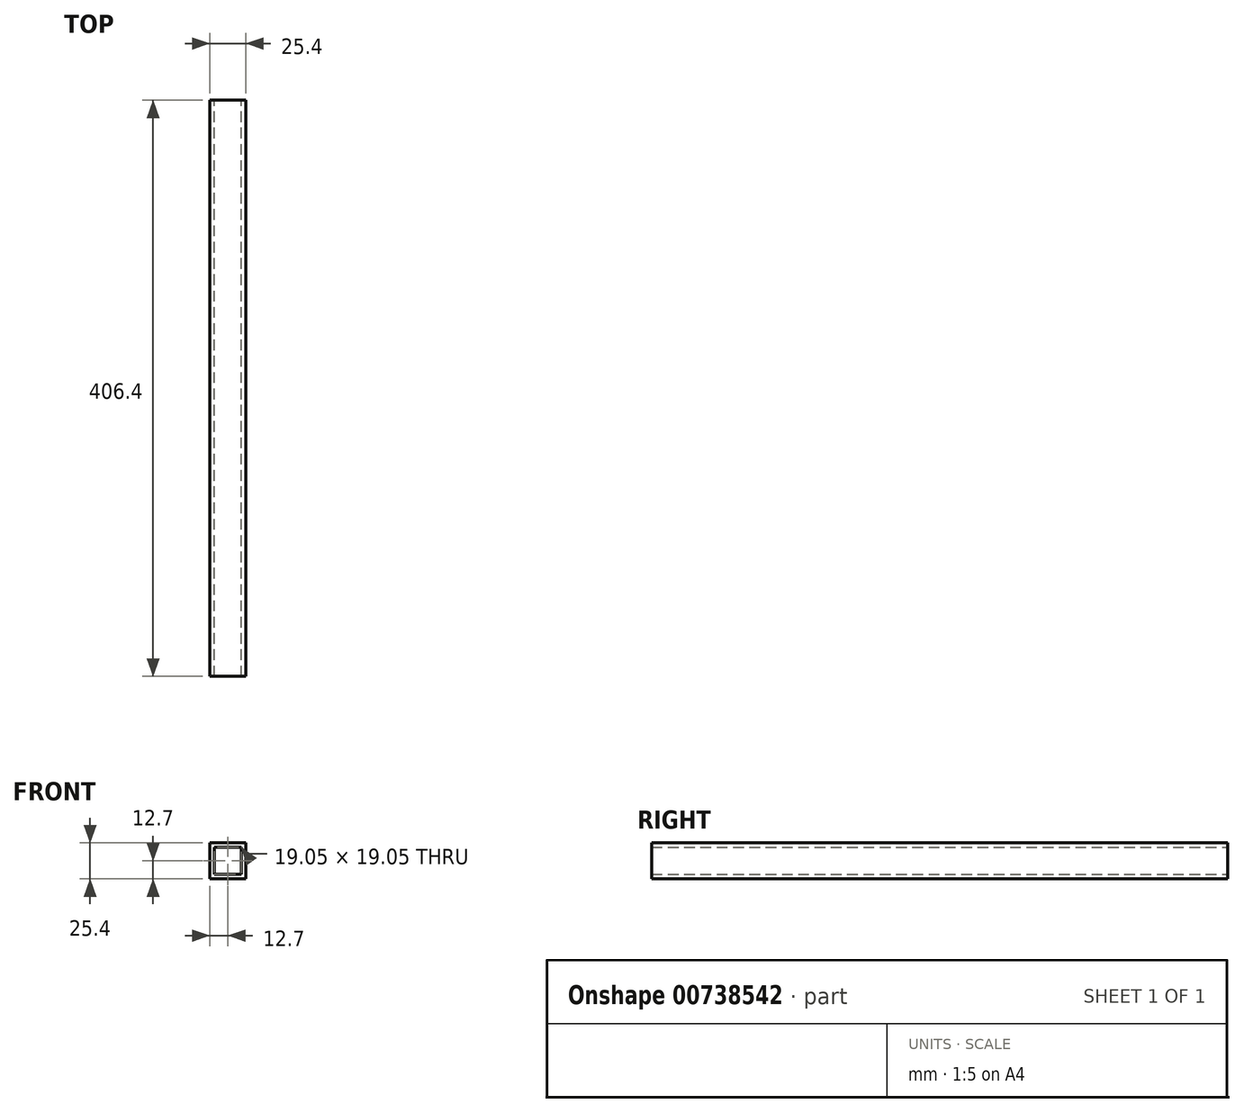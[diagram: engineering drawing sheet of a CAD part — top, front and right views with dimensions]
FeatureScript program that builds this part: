
annotation { "Feature Type Name" : "Feature", "Feature Type Description" : "" }
export const myFeature = defineFeature(function(context is Context, id is Id, definition is map)
    precondition{}
    {
        {
            var Q0;
            Q0=qCreatedBy(makeId("Front.planeOp"),FACE);
            var sketch = newSketch(context, id + "F0", { "sketchPlane" : qUnion([Q0])});
            skLineSegment(sketch, "E0.bottom", {"start": v(12.7, 12.7) * mm, "end": v(-12.7, 12.7) * mm});
            skLineSegment(sketch, "E0.top", {"start": v(12.7, -12.7) * mm, "end": v(-12.7, -12.7) * mm});
            skLineSegment(sketch, "E0.left", {"start": v(12.7, 12.7) * mm, "end": v(12.7, -12.7) * mm});
            skLineSegment(sketch, "E0.right", {"start": v(-12.7, 12.7) * mm, "end": v(-12.7, -12.7) * mm});
            skPoint(sketch, "E0.middle", {"position": v(0, 0) * mm});
            skLineSegment(sketch, "E1.0", {"start": v(-9.53, 9.53) * mm, "end": v(-9.53, -9.52) * mm});
            skLineSegment(sketch, "E1.1", {"start": v(9.52, 9.53) * mm, "end": v(-9.53, 9.53) * mm});
            skLineSegment(sketch, "E1.2", {"start": v(9.53, 9.53) * mm, "end": v(9.53, -9.52) * mm});
            skLineSegment(sketch, "E1.3", {"start": v(9.53, -9.52) * mm, "end": v(-9.53, -9.52) * mm});
            skSolve(sketch);
        }
        {
            var Q0;
            Q0=qSketchRegion(id+"F0",true);
            extrude(context, id + "F1", {"entities" : qUnion([Q0]), "depth" : 406.4 * mm, "offsetDistance" : 25.4 * mm});
        }
    });
